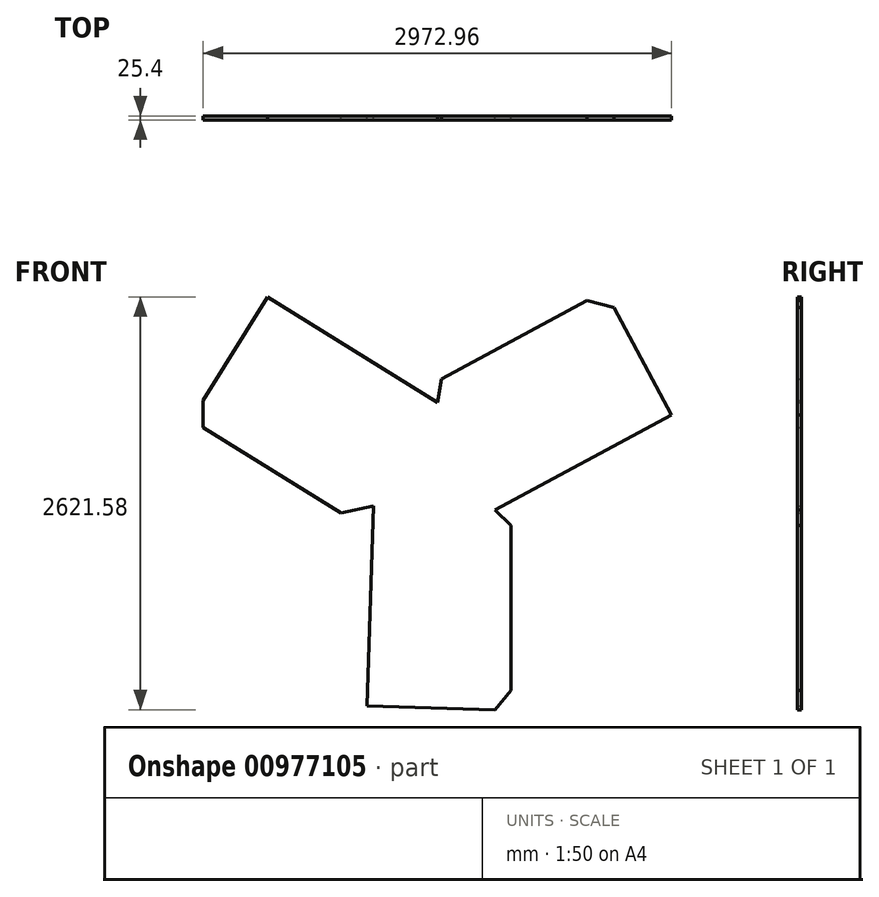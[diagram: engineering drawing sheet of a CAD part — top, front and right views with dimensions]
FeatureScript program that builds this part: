
annotation { "Feature Type Name" : "Feature", "Feature Type Description" : "" }
export const myFeature = defineFeature(function(context is Context, id is Id, definition is map)
    precondition{}
    {
        {
            var Q0;
            Q0=qCreatedBy(makeId("Front.planeOp"),FACE);
            var sketch = newSketch(context, id + "F0", { "sketchPlane" : qUnion([Q0])});
            skLineSegment(sketch, "E0", {"start": v(0, 352.52) * mm, "end": v(-408.05, -306) * mm});
            skLineSegment(sketch, "E1", {"start": v(-408.05, -306) * mm, "end": v(366.27, -330.12) * mm});
            skLineSegment(sketch, "E2", {"start": v(366.27, -330.12) * mm, "end": v(0, 352.52) * mm});
            skLineSegment(sketch, "E3", {"start": v(0, 352.52) * mm, "end": v(1119.09, 952.97) * mm});
            skLineSegment(sketch, "E4", {"start": v(366.27, -330.12) * mm, "end": v(1485.36, 270.33) * mm});
            skLineSegment(sketch, "E5", {"start": v(1119.09, 952.97) * mm, "end": v(1485.36, 270.33) * mm});
            skLineSegment(sketch, "E6", {"start": v(0, 352.52) * mm, "end": v(-1079.55, 1021.46) * mm});
            skLineSegment(sketch, "E7", {"start": v(-408.05, -306) * mm, "end": v(-1487.6, 362.93) * mm});
            skLineSegment(sketch, "E8", {"start": v(-1487.6, 362.93) * mm, "end": v(-1079.55, 1021.46) * mm});
            skLineSegment(sketch, "E9", {"start": v(-408.05, -306) * mm, "end": v(-447.6, -1575.39) * mm});
            skLineSegment(sketch, "E10", {"start": v(366.27, -330.12) * mm, "end": v(366.27, -1600.12) * mm});
            skLineSegment(sketch, "E11", {"start": v(-447.6, -1575.39) * mm, "end": v(366.27, -1600.12) * mm});
            skLineSegment(sketch, "E12", {"start": v(-1487.6, 362.93) * mm, "end": v(-1487.6, 192.44) * mm});
            skLineSegment(sketch, "E13", {"start": v(-1487.6, 192.44) * mm, "end": v(-613.4, -349.25) * mm});
            skLineSegment(sketch, "E14", {"start": v(-613.4, -349.25) * mm, "end": v(-408.05, -306) * mm});
            skLineSegment(sketch, "E15", {"start": v(0, 352.52) * mm, "end": v(25.8, 501.3) * mm});
            skLineSegment(sketch, "E16", {"start": v(25.8, 501.3) * mm, "end": v(950, 997.17) * mm});
            skLineSegment(sketch, "E17", {"start": v(950, 997.17) * mm, "end": v(1119.09, 952.97) * mm});
            skLineSegment(sketch, "E18", {"start": v(366.27, -330.12) * mm, "end": v(466.1, -431.48) * mm});
            skLineSegment(sketch, "E19", {"start": v(466.1, -431.48) * mm, "end": v(466.1, -1478.4) * mm});
            skLineSegment(sketch, "E20", {"start": v(466.1, -1478.4) * mm, "end": v(366.27, -1600.12) * mm});
            skSolve(sketch);
        }
        {
            var Q0;
            Q0 = qSketchRegion(id + "F0", true);
            extrude(context, id + "F1", {"entities" : qUnion([Q0]), "depth" : 25.4 * mm, "offsetDistance" : 25.4 * mm});
        }
    });
